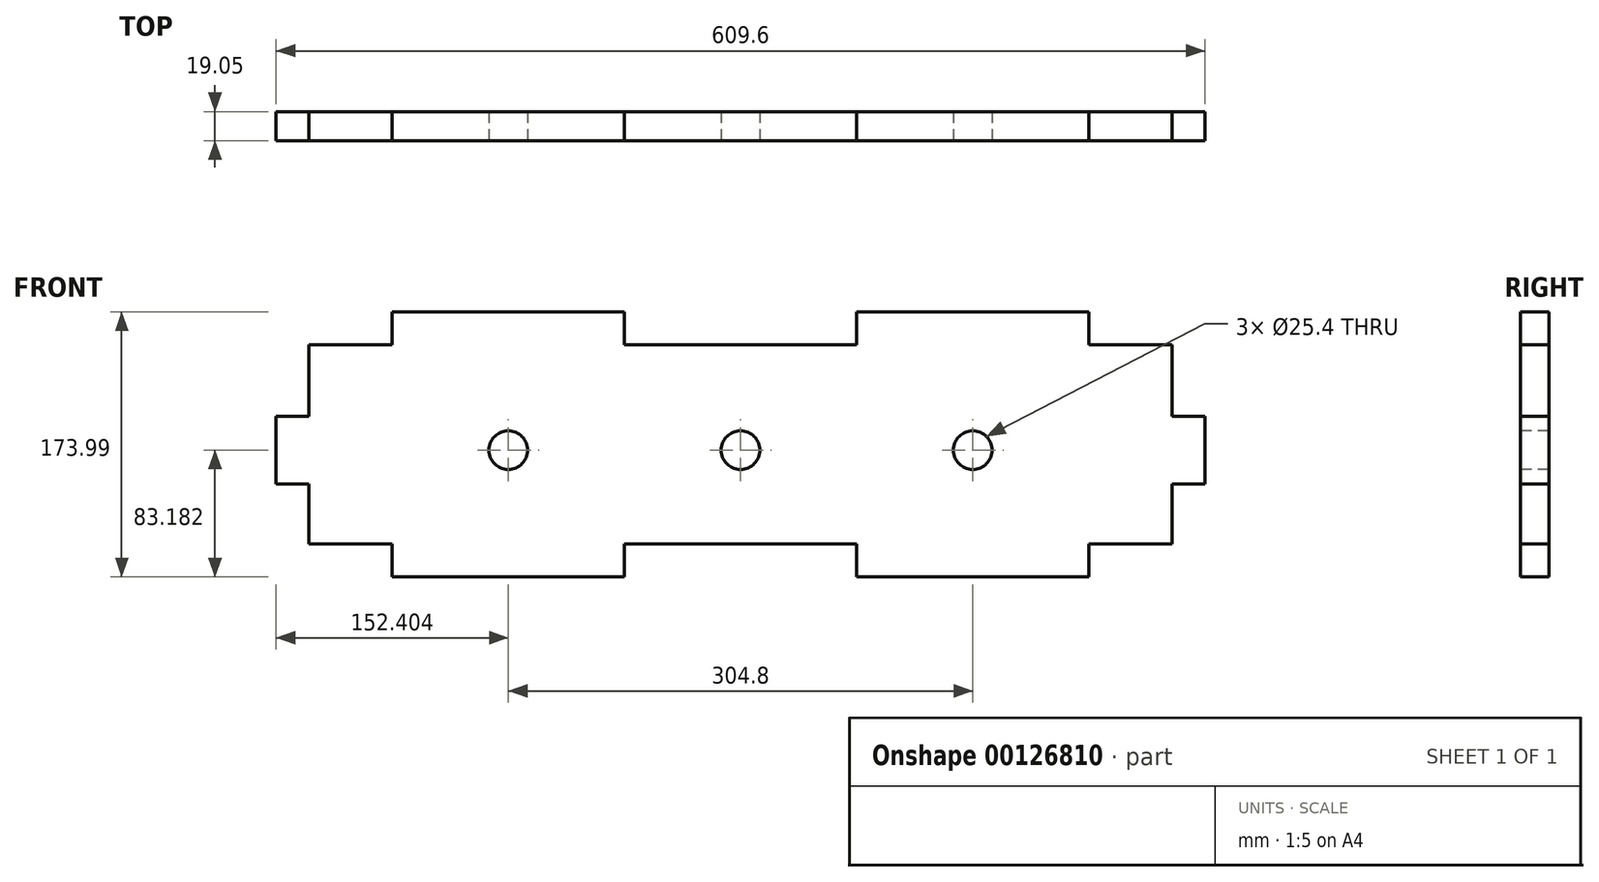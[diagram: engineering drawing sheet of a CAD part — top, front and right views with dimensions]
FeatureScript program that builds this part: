
annotation { "Feature Type Name" : "Feature", "Feature Type Description" : "" }
export const myFeature = defineFeature(function(context is Context, id is Id, definition is map)
    precondition{}
    {
        {
            var Q0;
            Q0=qCreatedBy(makeId("Front.planeOp"),FACE);
            var sketch = newSketch(context, id + "F0", { "sketchPlane" : qUnion([Q0])});
            skLineSegment(sketch, "E0", {"start": v(-86.79, 17.86) * mm, "end": v(-65.2, 17.86) * mm});
            skLineSegment(sketch, "E1", {"start": v(-65.2, 17.86) * mm, "end": v(-65.2, -21.51) * mm});
            skLineSegment(sketch, "E2", {"start": v(-65.2, -21.51) * mm, "end": v(-10.59, -21.51) * mm});
            skLineSegment(sketch, "E3", {"start": v(501.22, -21.51) * mm, "end": v(501.22, 17.86) * mm});
            skLineSegment(sketch, "E4", {"start": v(501.22, 17.86) * mm, "end": v(522.81, 17.86) * mm});
            skLineSegment(sketch, "E5", {"start": v(522.81, 17.86) * mm, "end": v(522.81, 62.3) * mm});
            skLineSegment(sketch, "E6", {"start": v(522.81, 62.3) * mm, "end": v(501.22, 62.3) * mm});
            skLineSegment(sketch, "E7", {"start": v(-86.79, 62.3) * mm, "end": v(-86.79, 17.86) * mm});
            skLineSegment(sketch, "E8.0", {"start": v(-10.59, -43.1) * mm, "end": v(141.81, -43.1) * mm});
            skLineSegment(sketch, "E9.0", {"start": v(-10.59, -21.51) * mm, "end": v(-10.59, -43.1) * mm});
            skLineSegment(sketch, "E10.0", {"start": v(141.81, -21.51) * mm, "end": v(141.81, -43.1) * mm});
            skLineSegment(sketch, "E11.0", {"start": v(294.21, -21.51) * mm, "end": v(294.21, -43.1) * mm});
            skLineSegment(sketch, "E12.0", {"start": v(446.61, -21.51) * mm, "end": v(446.61, -43.1) * mm});
            skLineSegment(sketch, "E13.trimOffspring", {"start": v(294.21, -43.1) * mm, "end": v(446.61, -43.1) * mm});
            skLineSegment(sketch, "E14.trimOffspring", {"start": v(141.81, -21.51) * mm, "end": v(294.21, -21.51) * mm});
            skLineSegment(sketch, "E15.trimOffspring", {"start": v(446.61, -21.51) * mm, "end": v(501.22, -21.51) * mm});
            skLineSegment(sketch, "E16.top", {"start": v(-65.2, 109.3) * mm, "end": v(-10.59, 109.3) * mm});
            skLineSegment(sketch, "E16.left", {"start": v(-65.2, 62.3) * mm, "end": v(-65.2, 109.3) * mm});
            skLineSegment(sketch, "E16.right", {"start": v(501.22, 62.3) * mm, "end": v(501.22, 109.3) * mm});
            skLineSegment(sketch, "E17.trimOffspring", {"start": v(-65.2, 62.3) * mm, "end": v(-86.79, 62.3) * mm});
            skLineSegment(sketch, "E18.MirrorCS", {"start": v(141.81, 109.3) * mm, "end": v(141.81, 130.89) * mm});
            skLineSegment(sketch, "E19.MirrorCS", {"start": v(-10.59, 130.89) * mm, "end": v(141.81, 130.89) * mm});
            skLineSegment(sketch, "E20.MirrorCS", {"start": v(-10.59, 109.3) * mm, "end": v(-10.59, 130.89) * mm});
            skLineSegment(sketch, "E21.MirrorCS", {"start": v(294.21, 109.3) * mm, "end": v(294.21, 130.89) * mm});
            skLineSegment(sketch, "E22.MirrorCS", {"start": v(294.21, 130.89) * mm, "end": v(446.61, 130.89) * mm});
            skLineSegment(sketch, "E23.MirrorCS", {"start": v(446.61, 109.3) * mm, "end": v(446.61, 130.89) * mm});
            skPoint(sketch, "E24.start.orphan", {"position": v(218.01, 43.9) * mm});
            skPoint(sketch, "E25.orphan", {"position": v(218.01, 109.3) * mm});
            skPoint(sketch, "E26.start.orphan", {"position": v(218.01, -21.51) * mm});
            skLineSegment(sketch, "E27.trimOffspring", {"start": v(446.61, 109.3) * mm, "end": v(501.22, 109.3) * mm});
            skLineSegment(sketch, "E28.trimOffspring", {"start": v(141.81, 109.3) * mm, "end": v(294.21, 109.3) * mm});
            skSolve(sketch);
        }
        {
            var Q0;
            Q0 = qSketchRegion(id + "F0", true);
            extrude(context, id + "F1", {"entities" : qUnion([Q0]), "depth" : 19.05 * mm});
        }
        {
            var Q0;
            Q0=makeQuery(id+"F1.opExtrude","CAP_FACE",FACE,{"disambiguationData":[OSD([sQuery(id+"F0.wireOp",EDGE,"E0"),sQuery(id+"F0.wireOp",EDGE,"E1"),sQuery(id+"F0.wireOp",EDGE,"E2"),sQuery(id+"F0.wireOp",EDGE,"E3"),sQuery(id+"F0.wireOp",EDGE,"E4"),sQuery(id+"F0.wireOp",EDGE,"E5"),sQuery(id+"F0.wireOp",EDGE,"E6"),sQuery(id+"F0.wireOp",EDGE,"E7"),sQuery(id+"F0.wireOp",EDGE,"E8.0"),sQuery(id+"F0.wireOp",EDGE,"E9.0"),sQuery(id+"F0.wireOp",EDGE,"E10.0"),sQuery(id+"F0.wireOp",EDGE,"E11.0"),sQuery(id+"F0.wireOp",EDGE,"E12.0"),sQuery(id+"F0.wireOp",EDGE,"E13.trimOffspring"),sQuery(id+"F0.wireOp",EDGE,"E14.trimOffspring"),sQuery(id+"F0.wireOp",EDGE,"E15.trimOffspring"),sQuery(id+"F0.wireOp",EDGE,"E16.top"),sQuery(id+"F0.wireOp",EDGE,"E16.left"),sQuery(id+"F0.wireOp",EDGE,"E16.right"),sQuery(id+"F0.wireOp",EDGE,"E17.trimOffspring"),sQuery(id+"F0.wireOp",EDGE,"E18.MirrorCS"),sQuery(id+"F0.wireOp",EDGE,"E19.MirrorCS"),sQuery(id+"F0.wireOp",EDGE,"E20.MirrorCS"),sQuery(id+"F0.wireOp",EDGE,"E21.MirrorCS"),sQuery(id+"F0.wireOp",EDGE,"E22.MirrorCS"),sQuery(id+"F0.wireOp",EDGE,"E23.MirrorCS"),sQuery(id+"F0.wireOp",EDGE,"E27.trimOffspring"),sQuery(id+"F0.wireOp",EDGE,"E28.trimOffspring")])],"isStart":false});
            var sketch = newSketch(context, id + "F2", { "sketchPlane" : qUnion([Q0])});
            skCircle(sketch, "E29", {"center": v(65.61, 40.08) * mm, "radius": 12.7 * mm});
            skPoint(sketch, "E29.centerSnap0", {"position": v(-86.79, 40.08) * mm});
            skPoint(sketch, "E29.centerSnap1", {"position": v(65.61, -43.1) * mm});
            skCircle(sketch, "E30", {"center": v(218.01, 40.08) * mm, "radius": 12.7 * mm});
            skPoint(sketch, "E30.centerSnap0", {"position": v(218.01, -21.51) * mm});
            skCircle(sketch, "E31", {"center": v(370.41, 40.08) * mm, "radius": 12.7 * mm});
            skPoint(sketch, "E31.centerSnap0", {"position": v(370.41, -43.1) * mm});
            skSolve(sketch);
        }
        {
            var Q0;
            Q0 = qSketchRegion(id + "F2", true);
            extrude(context, id + "F3", {"entities" : qUnion([Q0]), "operationType" : NewBodyOperationType.REMOVE, "endBound" : BoundingType.THROUGH_ALL, "oppositeDirection" : true, "depth" : 25.4 * mm});
        }
    });
